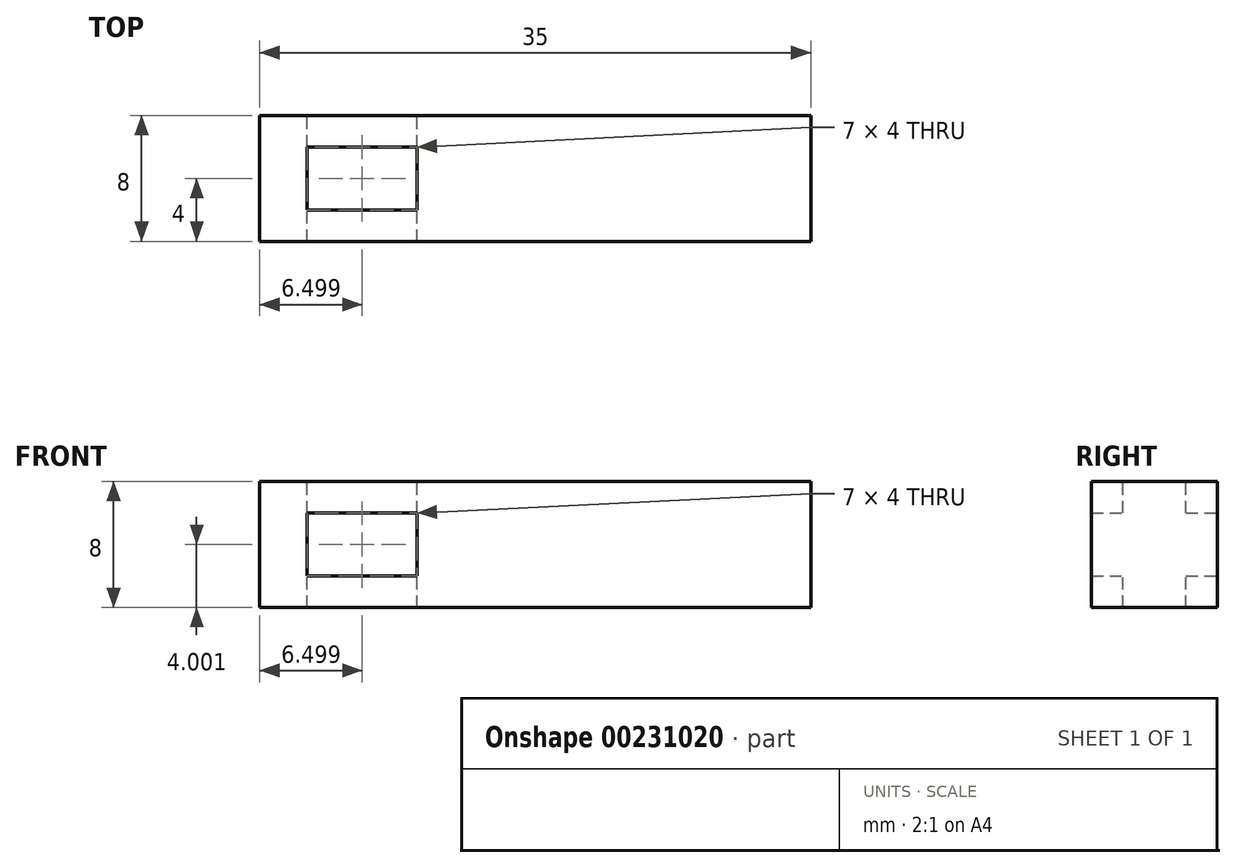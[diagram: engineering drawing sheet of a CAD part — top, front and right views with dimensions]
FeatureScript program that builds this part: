
annotation { "Feature Type Name" : "Feature", "Feature Type Description" : "" }
export const myFeature = defineFeature(function(context is Context, id is Id, definition is map)
    precondition{}
    {
        {
            var Q0;
            Q0=qCreatedBy(makeId("Front.planeOp"),FACE);
            var sketch = newSketch(context, id + "F0", { "sketchPlane" : qUnion([Q0])});
            skLineSegment(sketch, "E0.bottom", {"start": v(-42.35, 39.21) * mm, "end": v(-7.35, 39.21) * mm});
            skLineSegment(sketch, "E0.top", {"start": v(-42.35, 31.21) * mm, "end": v(-7.35, 31.21) * mm});
            skLineSegment(sketch, "E0.left", {"start": v(-42.35, 39.21) * mm, "end": v(-42.35, 31.21) * mm});
            skLineSegment(sketch, "E0.right", {"start": v(-7.35, 39.21) * mm, "end": v(-7.35, 31.21) * mm});
            skLineSegment(sketch, "E1.0", {"start": v(-39.35, 37.21) * mm, "end": v(-32.35, 37.21) * mm});
            skLineSegment(sketch, "E2.0", {"start": v(-39.35, 33.21) * mm, "end": v(-32.35, 33.21) * mm});
            skLineSegment(sketch, "E3.0", {"start": v(-39.35, 37.21) * mm, "end": v(-39.35, 33.21) * mm});
            skLineSegment(sketch, "E4.trimOffspring", {"start": v(-32.35, 37.21) * mm, "end": v(-32.35, 33.21) * mm});
            skSolve(sketch);
        }
        {
            var Q0;
            Q0 = qSketchRegion(id + "F0", true);
            extrude(context, id + "F1", {"entities" : qUnion([Q0]), "depth" : 8 * mm});
        }
        {
            var Q0;
            Q0=makeQuery(id+"F1.opExtrude","SWEPT_FACE",FACE,{"disambiguationData":[OSD([sQuery(id+"F0.wireOp",EDGE,"E0.bottom")])]});
            var sketch = newSketch(context, id + "F2", { "sketchPlane" : qUnion([Q0])});
            skLineSegment(sketch, "E5.bottom", {"start": v(-39.35, -2) * mm, "end": v(-32.35, -2) * mm});
            skLineSegment(sketch, "E5.top", {"start": v(-39.35, -6) * mm, "end": v(-32.35, -6) * mm});
            skLineSegment(sketch, "E5.left", {"start": v(-39.35, -2) * mm, "end": v(-39.35, -6) * mm});
            skLineSegment(sketch, "E5.right", {"start": v(-32.35, -2) * mm, "end": v(-32.35, -6) * mm});
            skSolve(sketch);
        }
        {
            var Q0;
            Q0=makeQuery(id+"F2.imprint","IMPRINT",FACE,{"disambiguationData":[TD([[makeQuery(id+"F2.imprint","IMPRINT",EDGE,{"derivedFrom":sQuery(id+"F2.wireOp",EDGE,"E5.bottom")}),-1.0]])]});
            extrude(context, id + "F3", {"entities" : qUnion([Q0]), "operationType" : NewBodyOperationType.REMOVE, "oppositeDirection" : true, "depth" : 25 * mm});
        }
    });
